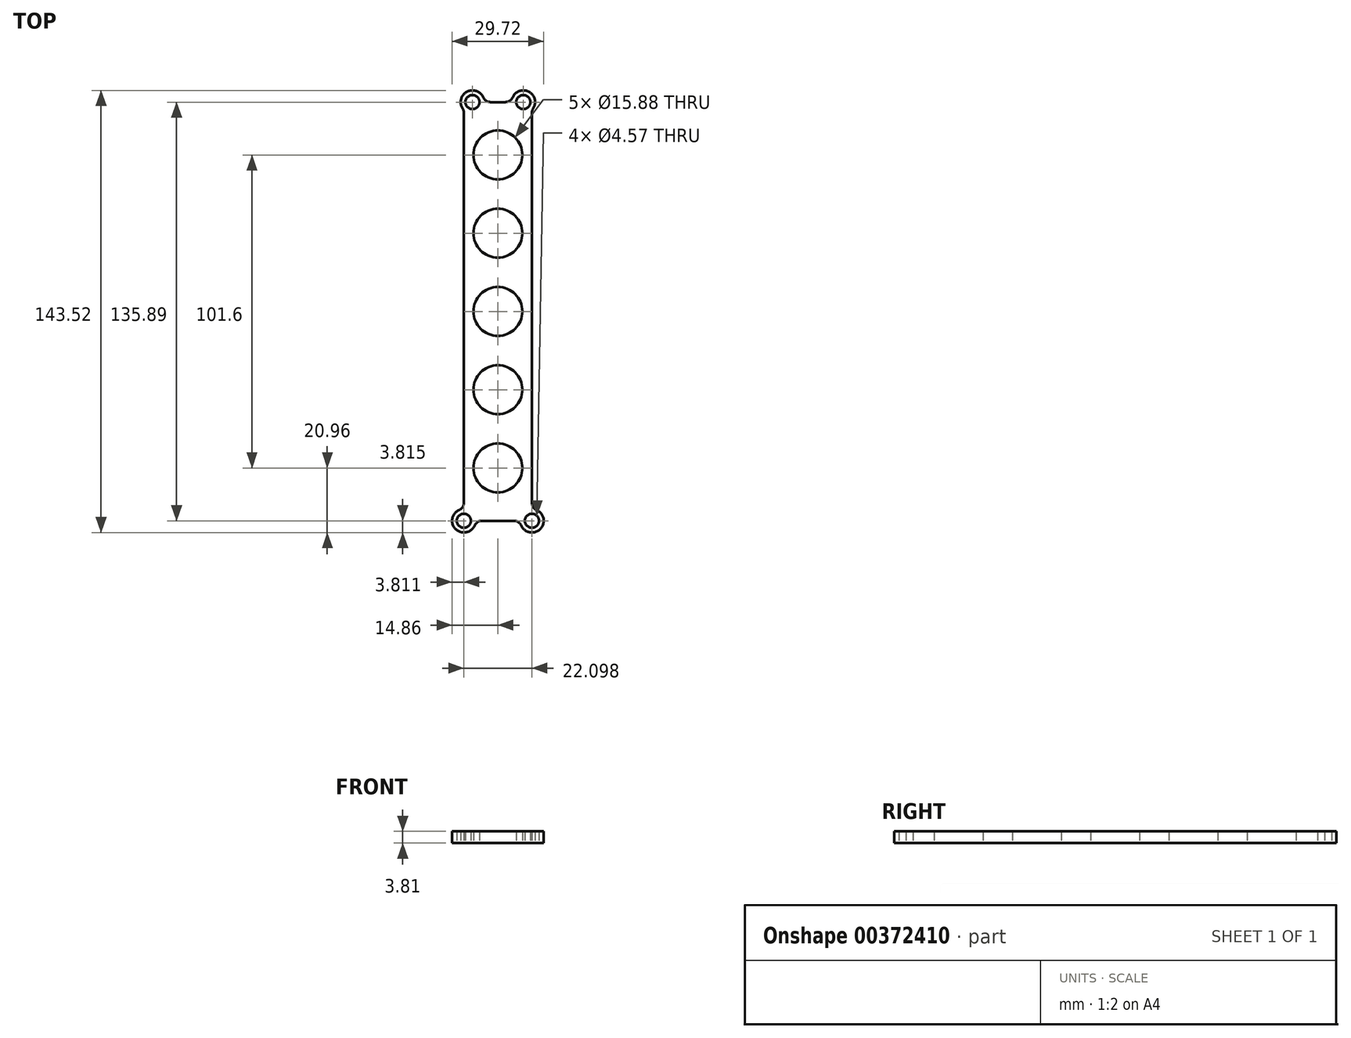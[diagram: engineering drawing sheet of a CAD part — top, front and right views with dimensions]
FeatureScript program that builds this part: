
annotation { "Feature Type Name" : "Feature", "Feature Type Description" : "" }
export const myFeature = defineFeature(function(context is Context, id is Id, definition is map)
    precondition{}
    {
        {
            var Q0;
            Q0=qCreatedBy(makeId("Top.planeOp"),FACE);
            var sketch = newSketch(context, id + "F0", { "sketchPlane" : qUnion([Q0])});
            skLineSegment(sketch, "E0.bottom", {"start": v(-2.44, 67.95) * mm, "end": v(2.44, 67.95) * mm});
            skLineSegment(sketch, "E0.top", {"start": v(-5.23, -67.95) * mm, "end": v(5.23, -67.95) * mm});
            skLineSegment(sketch, "E0.left", {"start": v(-11.05, 64.5) * mm, "end": v(-11.05, -62.13) * mm});
            skLineSegment(sketch, "E0.right", {"start": v(11.05, 64.5) * mm, "end": v(11.05, -62.13) * mm});
            skArc(sketch, "E1", {"start": v(-12.57, -64.45) * mm, "mid": v(-13.74, -70.64) * mm, "end": v(-7.56, -69.47) * mm});
            skArc(sketch, "E2", {"start": v(7.56, -69.47) * mm, "mid": v(13.74, -70.64) * mm, "end": v(12.57, -64.45) * mm});
            skCircle(sketch, "E3", {"center": v(-11.05, -67.95) * mm, "radius": 2.29 * mm});
            skCircle(sketch, "E4", {"center": v(11.05, -67.95) * mm, "radius": 2.29 * mm});
            skPoint(sketch, "E5", {"position": v(0, 0) * mm});
            skPoint(sketch, "E6.visualSharp", {"position": v(-7.24, 67.95) * mm});
            skPoint(sketch, "E7.visualSharp", {"position": v(-11.05, 82.88) * mm});
            skPoint(sketch, "E8.visualSharp", {"position": v(7.24, 67.95) * mm});
            skPoint(sketch, "E9.visualSharp", {"position": v(11.05, 45.4) * mm});
            skPoint(sketch, "E10.visualSharp", {"position": v(-11.05, -64.14) * mm});
            skArc(sketch, "E10.filletArc", {"start": v(-12.57, -64.45) * mm, "mid": v(-11.46, -63.52) * mm, "end": v(-11.05, -62.13) * mm});
            skPoint(sketch, "E11.visualSharp", {"position": v(-7.24, -67.95) * mm});
            skArc(sketch, "E11.filletArc", {"start": v(-5.23, -67.94) * mm, "mid": v(-6.62, -68.36) * mm, "end": v(-7.56, -69.47) * mm});
            skPoint(sketch, "E12.visualSharp", {"position": v(7.24, -67.95) * mm});
            skArc(sketch, "E12.filletArc", {"start": v(7.56, -69.47) * mm, "mid": v(6.62, -68.36) * mm, "end": v(5.23, -67.94) * mm});
            skPoint(sketch, "E13.visualSharp", {"position": v(11.05, -64.14) * mm});
            skArc(sketch, "E13.filletArc", {"start": v(11.05, -62.13) * mm, "mid": v(11.46, -63.52) * mm, "end": v(12.57, -64.45) * mm});
            skLineSegment(sketch, "E14", {"start": v(0, 67.95) * mm, "end": v(0, -67.95) * mm, "construction": true});
            skCircle(sketch, "E15", {"center": v(0, 50.8) * mm, "radius": 7.94 * mm});
            skCircle(sketch, "E16", {"center": v(0, 25.4) * mm, "radius": 7.94 * mm});
            skCircle(sketch, "E17", {"center": v(0, 0) * mm, "radius": 7.94 * mm});
            skCircle(sketch, "E18", {"center": v(0, -25.4) * mm, "radius": 7.94 * mm});
            skCircle(sketch, "E19", {"center": v(0, -50.8) * mm, "radius": 7.94 * mm});
            skCircle(sketch, "E20", {"center": v(-8.26, 67.95) * mm, "radius": 2.29 * mm});
            skCircle(sketch, "E21", {"center": v(8.25, 67.95) * mm, "radius": 2.29 * mm});
            skPoint(sketch, "E22", {"position": v(0, 67.95) * mm});
            skArc(sketch, "E23", {"start": v(-4.76, 69.47) * mm, "mid": v(-10.06, 71.3) * mm, "end": v(-11.46, 65.88) * mm});
            skArc(sketch, "E24", {"start": v(11.46, 65.88) * mm, "mid": v(10.06, 71.3) * mm, "end": v(4.76, 69.47) * mm});
            skPoint(sketch, "E25.visualSharp", {"position": v(-11.05, 65.35) * mm});
            skArc(sketch, "E25.filletArc", {"start": v(-11.05, 64.5) * mm, "mid": v(-11.15, 65.22) * mm, "end": v(-11.46, 65.88) * mm});
            skPoint(sketch, "E26.visualSharp", {"position": v(11.05, 65.35) * mm});
            skArc(sketch, "E26.filletArc", {"start": v(11.46, 65.88) * mm, "mid": v(11.15, 65.22) * mm, "end": v(11.05, 64.5) * mm});
            skPoint(sketch, "E27.newPointB", {"position": v(-5.23, 67.95) * mm});
            skArc(sketch, "E27.filletArc", {"start": v(-4.76, 69.47) * mm, "mid": v(-3.83, 68.36) * mm, "end": v(-2.44, 67.94) * mm});
            skPoint(sketch, "E28.newPointA", {"position": v(5.23, 67.95) * mm});
            skArc(sketch, "E28.filletArc", {"start": v(2.44, 67.94) * mm, "mid": v(3.83, 68.36) * mm, "end": v(4.76, 69.47) * mm});
            skLineSegment(sketch, "E29", {"start": v(-8.26, 73.3) * mm, "end": v(-8.26, 67.95) * mm, "construction": true});
            skLineSegment(sketch, "E30", {"start": v(-8.26, 73.3) * mm, "end": v(8.25, 73.3) * mm, "construction": true});
            skLineSegment(sketch, "E31", {"start": v(8.25, 67.95) * mm, "end": v(8.25, 73.3) * mm, "construction": true});
            skPoint(sketch, "E32", {"position": v(0, 73.3) * mm});
            skSolve(sketch);
        }
        {
            var Q0;
            Q0 = qSketchRegion(id + "F0", true);
            extrude(context, id + "F1", {"entities" : qUnion([Q0]), "depth" : 3.8 * mm});
        }
    });
